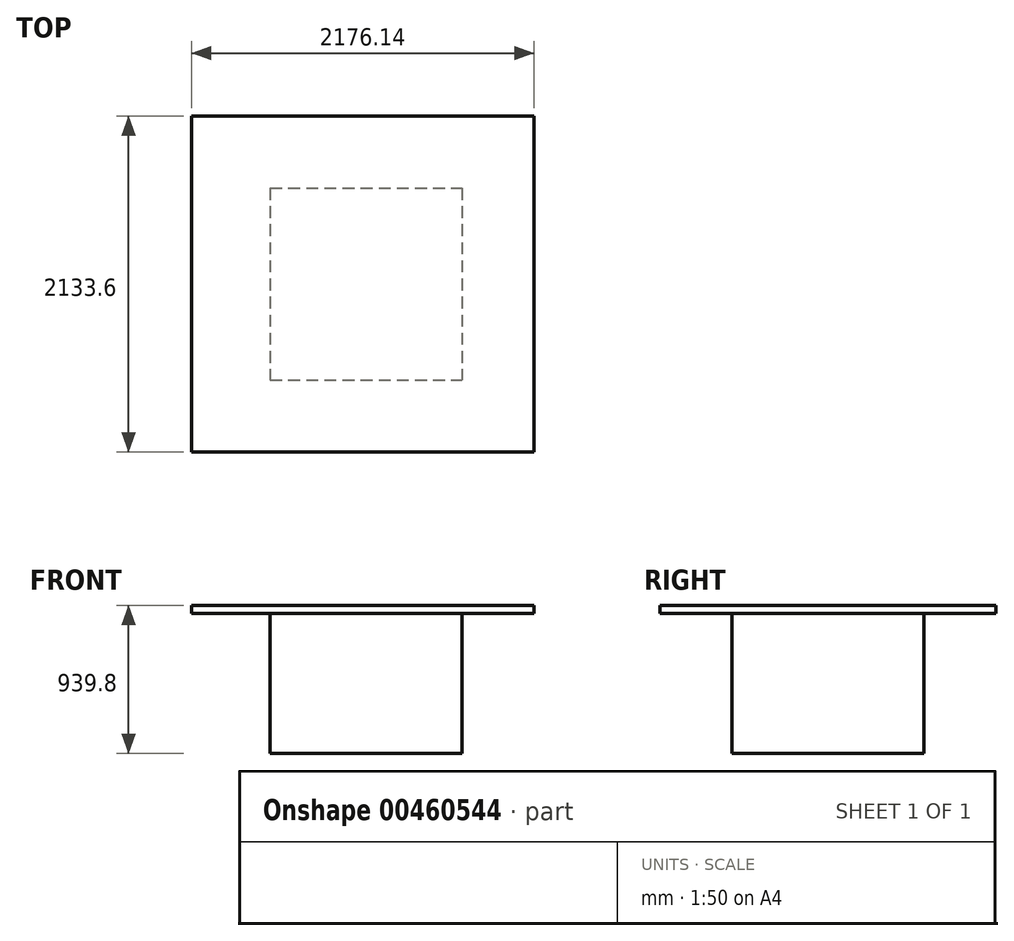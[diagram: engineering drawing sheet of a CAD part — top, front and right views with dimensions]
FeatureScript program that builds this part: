
annotation { "Feature Type Name" : "Feature", "Feature Type Description" : "" }
export const myFeature = defineFeature(function(context is Context, id is Id, definition is map)
    precondition{}
    {
        {
            var Q0;
            Q0=qCreatedBy(makeId("Top.planeOp"),FACE);
            var sketch = newSketch(context, id + "F0", { "sketchPlane" : qUnion([Q0])});
            skLineSegment(sketch, "E0.bottom", {"start": v(-588.33, 856.3) * mm, "end": v(630.87, 856.3) * mm});
            skLineSegment(sketch, "E0.top", {"start": v(-588.33, -362.9) * mm, "end": v(630.87, -362.9) * mm});
            skLineSegment(sketch, "E0.left", {"start": v(-588.33, 856.3) * mm, "end": v(-588.33, -362.9) * mm});
            skLineSegment(sketch, "E0.right", {"start": v(630.87, 856.3) * mm, "end": v(630.87, -362.9) * mm});
            skSolve(sketch);
        }
        {
            var Q0;
            Q0 = qSketchRegion(id + "F0", true);
            extrude(context, id + "F1", {"entities" : qUnion([Q0]), "depth" : 889 * mm});
        }
        {
            var Q0;
            Q0=makeQuery(id+"F1.opExtrude","CAP_FACE",FACE,{"disambiguationData":[OSD([sQuery(id+"F0.wireOp",EDGE,"E0.bottom"),sQuery(id+"F0.wireOp",EDGE,"E0.top"),sQuery(id+"F0.wireOp",EDGE,"E0.left"),sQuery(id+"F0.wireOp",EDGE,"E0.right")])],"isStart":false});
            var sketch = newSketch(context, id + "F2", { "sketchPlane" : qUnion([Q0])});
            skLineSegment(sketch, "E1.bottom", {"start": v(-1088.07, 1313.5) * mm, "end": v(1088.07, 1313.5) * mm});
            skLineSegment(sketch, "E1.top", {"start": v(-1088.07, -820.1) * mm, "end": v(1088.07, -820.1) * mm});
            skLineSegment(sketch, "E1.left", {"start": v(-1088.07, 1313.5) * mm, "end": v(-1088.07, -820.1) * mm});
            skLineSegment(sketch, "E1.right", {"start": v(1088.07, 1313.5) * mm, "end": v(1088.07, -820.1) * mm});
            skPoint(sketch, "E1.middle", {"position": v(0, 246.7) * mm});
            skPoint(sketch, "E1.middle.positionSnap0", {"position": v(-588.33, 246.7) * mm});
            skPoint(sketch, "E1.centerSnap0", {"position": v(-588.33, 246.7) * mm});
            skSolve(sketch);
        }
        {
            var Q0;
            Q0 = qSketchRegion(id + "F2", true);
            extrude(context, id + "F3", {"entities" : qUnion([Q0]), "operationType" : NewBodyOperationType.ADD, "depth" : 50.8 * mm});
        }
    });
